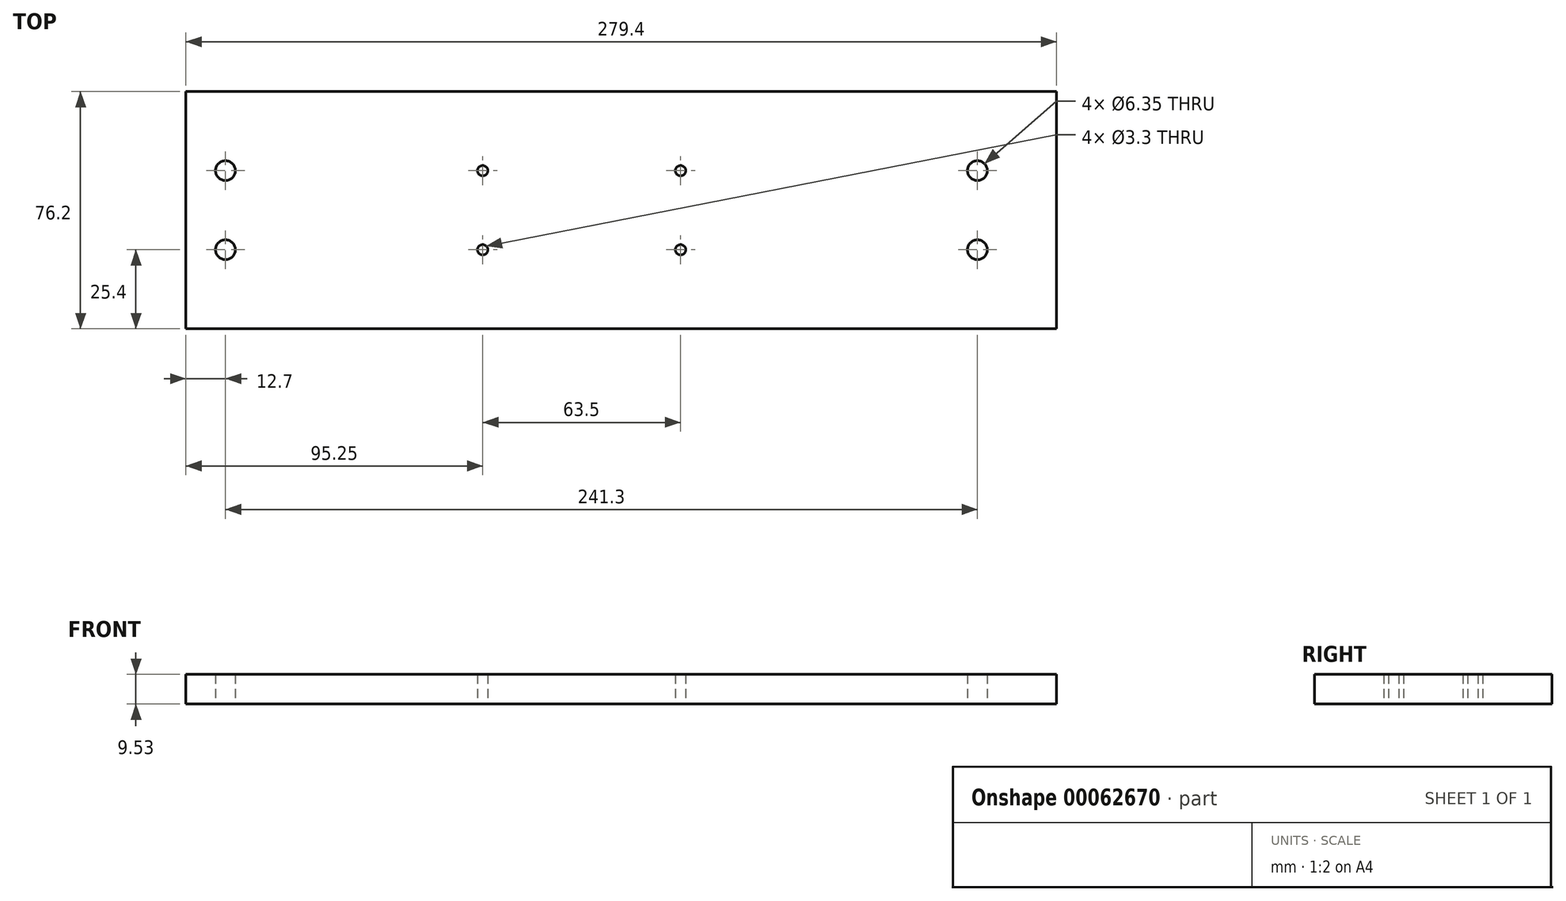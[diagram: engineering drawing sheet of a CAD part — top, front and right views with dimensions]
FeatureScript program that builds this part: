
annotation { "Feature Type Name" : "Feature", "Feature Type Description" : "" }
export const myFeature = defineFeature(function(context is Context, id is Id, definition is map)
    precondition{}
    {
        {
            var Q0;
            Q0=qCreatedBy(makeId("Top.planeOp"),FACE);
            var sketch = newSketch(context, id + "F0", { "sketchPlane" : qUnion([Q0])});
            skLineSegment(sketch, "E0.bottom", {"start": v(0, 0) * mm, "end": v(279.4, 0) * mm});
            skLineSegment(sketch, "E0.top", {"start": v(0, 76.2) * mm, "end": v(279.4, 76.2) * mm});
            skLineSegment(sketch, "E0.left", {"start": v(0, 0) * mm, "end": v(0, 76.2) * mm});
            skLineSegment(sketch, "E0.right", {"start": v(279.4, 0) * mm, "end": v(279.4, 76.2) * mm});
            skCircle(sketch, "E1", {"center": v(12.7, 50.8) * mm, "radius": 3.18 * mm});
            skCircle(sketch, "E2", {"center": v(12.7, 25.4) * mm, "radius": 3.18 * mm});
            skCircle(sketch, "E3", {"center": v(95.25, 25.4) * mm, "radius": 1.65 * mm});
            skCircle(sketch, "E4", {"center": v(95.25, 50.8) * mm, "radius": 1.65 * mm});
            skCircle(sketch, "E5", {"center": v(158.75, 50.8) * mm, "radius": 1.65 * mm});
            skCircle(sketch, "E6", {"center": v(254, 50.8) * mm, "radius": 3.18 * mm});
            skCircle(sketch, "E7", {"center": v(254, 25.4) * mm, "radius": 3.18 * mm});
            skCircle(sketch, "E8", {"center": v(158.75, 25.4) * mm, "radius": 1.65 * mm});
            skSolve(sketch);
        }
        {
            var Q0;
            Q0=makeQuery(id+"F0.imprint","IMPRINT",FACE,{"disambiguationData":[TD([[makeQuery(id+"F0.imprint","IMPRINT",EDGE,{"derivedFrom":sQuery(id+"F0.wireOp",EDGE,"E0.bottom")}),1.0]])]});
            extrude(context, id + "F1", {"entities" : qUnion([Q0]), "depth" : 9.52 * mm});
        }
    });
